# Revit family: HVAC-Chilled_Beam-Dadanco-ACB55
name_source: partatom
category: Mechanical Equipment
revit_build: Autodesk Revit 2018 (Build: 20170223_1515(x64)
units: mm (PartAtom-declared; Revit-internal decimal feet)

## family parameters
Always vertical = Yes
Cut with Voids When Loaded = No
OmniClass Number = 23.75.70.17.31
OmniClass Title = Induction Units
Part Type = Normal
Room Calculation Point = No
Round Connector Dimension = Use Diameter
Shared = No
Work Plane-Based = No

## types (5) — shared parameters
2 Pipe Coil Configuration = Yes
2 or 4 pipe = 2
4 Pipe Coil Configuration = No
Assembly Code = D3040100
CWF = 0 GPM
CWPD = 0.00 ftH2O
Cooling Primary Air Dry Bulb = 0 °F
Cooling Primary Air Wet Bulb = 0 °F
Cooling Room Dry Bulb = 0 °F
Cooling Supply Air Temperature = 0 °F
Description = Active Chilled Beam
HWF = 0 GPM
HWPD = 0.00 ftH2O
Heating Primary Air Dry Bulb = 0 °F
Heating Room Dry Bulb = 0 °F
Heating Supply Air Temperature = 0 °F
Latent Cooling = 0.0 Btu/h
Manufacturer = Dadanco
Model = ACB55
Net Unit Cooling Sensible = 0.0 Btu/h
Net Unit Heating Sensible = 0.0 Btu/h
PA = 0 CFM
PASP = 0.00 in-wg
Pipe Coil Inlet = 2 Pipe Coi, 0.5 inch SWT Stub Coil Connection
Pipe Coil Outlet = 2 Pipe Coi, 0.5 inch SWT Stub Coil Connection
Pipe Material = Metal-Dadanco-Copper-Satin
Primary Air Inlet Size = 0' - 6"
Revision Date = 05/27/2021
SCHW Temp Out = 0 °F
SCHW Temperature = 0 °F
SHHW Temp Out = 0 °F
SHHW Temperature = 0 °F
Secondary Air Sensible Cooling = 0.0 Btu/h
Secondary Air Sensible Heating = 0.0 Btu/h
Supply Air = 0 CFM
Total Cooling Capacity = 0.0 Btu/h
Type Comments = 1-way Discharge Horizontal Coil, 1' Wide
URL = http://www.dadanco.com
Unit Height = 0' - 9 3/4"
Unit Width = 1' - 11 3/4"
zero-valued in all types: Cooling Room Relative Humidity

## per-type parameters (varying)
| type | Documentation Link | Housing Material | Keynote | Nominal Unit Length | Origin1 | Product Page URL | Unit Length | Unit Weight |
| 4' Nominal Length |  | Metal-Dadanco-Steel-Galvanized |  | 4' - 0" | 2' - 0" |  | 3' - 11 3/4" | 43 lb |
| 2' Nominal Length | http://www.dadanco.com | Metal-Dadanco-Steel-Galvanized | 23 37 00.A1 | 2' - 0" | 1' - 0" | http://www.activechilledbeam.com | 1' - 11 3/4" | 22 lb |
| 6' Nominal Length |  | Metal-Dadanco-Aluminum-Bone White | 23 37 00.A1 | 6' - 0" | 3' - 0" |  | 5' - 11 3/4" | 65 lb |
| 8' Nominal Length |  | Metal-Dadanco-Steel-Galvanized |  | 8' - 0" | 4' - 0" |  | 7' - 11 3/4" | 87 lb |
| 10' Nominal Length |  | Metal-Dadanco-Steel-Galvanized |  | 10' - 0" | 5' - 0" |  | 9' - 11 3/4" | 108 lb |

## geometry (parser evidence)
native form markers: Sweep x2
no freeform markers — native parametric forms only
